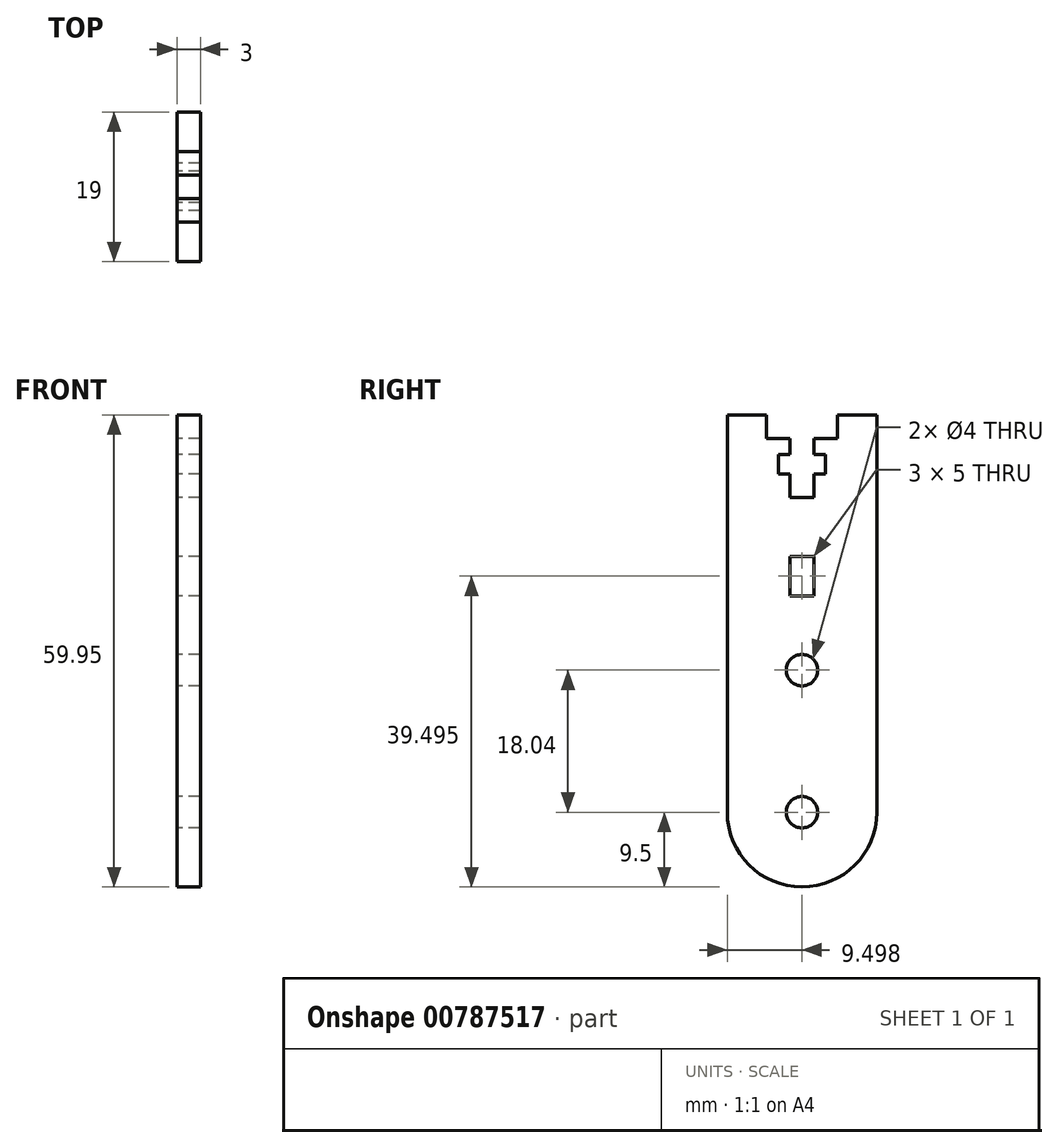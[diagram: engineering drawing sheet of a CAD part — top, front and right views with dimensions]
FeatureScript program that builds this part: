
annotation { "Feature Type Name" : "Feature", "Feature Type Description" : "" }
export const myFeature = defineFeature(function(context is Context, id is Id, definition is map)
    precondition{}
    {
        {
            var Q0;
            Q0=qCreatedBy(makeId("Right.planeOp"),FACE);
            var sketch = newSketch(context, id + "F0", { "sketchPlane" : qUnion([Q0])});
            skLineSegment(sketch, "E0.left", {"start": v(-56.6, 15.77) * mm, "end": v(-56.6, -34.68) * mm});
            skLineSegment(sketch, "E0.right", {"start": v(-37.6, 15.77) * mm, "end": v(-37.6, -34.68) * mm});
            skLineSegment(sketch, "E1", {"start": v(-56.6, 15.77) * mm, "end": v(-51.6, 15.77) * mm});
            skLineSegment(sketch, "E2", {"start": v(-51.6, 15.77) * mm, "end": v(-51.6, 12.77) * mm});
            skLineSegment(sketch, "E3", {"start": v(-51.6, 12.77) * mm, "end": v(-48.6, 12.77) * mm});
            skLineSegment(sketch, "E4", {"start": v(-48.6, 12.77) * mm, "end": v(-48.6, 10.77) * mm});
            skLineSegment(sketch, "E5", {"start": v(-48.6, 10.77) * mm, "end": v(-50.1, 10.77) * mm});
            skLineSegment(sketch, "E6", {"start": v(-50.1, 10.77) * mm, "end": v(-50.1, 8.27) * mm});
            skLineSegment(sketch, "E7", {"start": v(-50.1, 8.27) * mm, "end": v(-48.6, 8.27) * mm});
            skLineSegment(sketch, "E8", {"start": v(-48.6, 8.27) * mm, "end": v(-48.6, 5.27) * mm});
            skLineSegment(sketch, "E9", {"start": v(-48.6, 5.27) * mm, "end": v(-45.6, 5.27) * mm});
            skLineSegment(sketch, "E10", {"start": v(-45.6, 5.27) * mm, "end": v(-45.6, 8.27) * mm});
            skLineSegment(sketch, "E11", {"start": v(-45.6, 8.27) * mm, "end": v(-44.1, 8.27) * mm});
            skLineSegment(sketch, "E12", {"start": v(-44.1, 8.27) * mm, "end": v(-44.1, 10.77) * mm});
            skLineSegment(sketch, "E13", {"start": v(-44.1, 10.77) * mm, "end": v(-45.6, 10.77) * mm});
            skLineSegment(sketch, "E14", {"start": v(-45.6, 10.77) * mm, "end": v(-45.6, 12.77) * mm});
            skLineSegment(sketch, "E15", {"start": v(-45.6, 12.77) * mm, "end": v(-42.6, 12.77) * mm});
            skLineSegment(sketch, "E16", {"start": v(-42.6, 12.77) * mm, "end": v(-42.6, 15.77) * mm});
            skLineSegment(sketch, "E17", {"start": v(-42.6, 15.77) * mm, "end": v(-37.6, 15.77) * mm});
            skCircle(sketch, "E18", {"center": v(-47.1, -34.68) * mm, "radius": 2 * mm});
            skCircle(sketch, "E19", {"center": v(-47.1, -16.64) * mm, "radius": 2 * mm});
            skArc(sketch, "E20", {"start": v(-56.6, -34.68) * mm, "mid": v(-47.1, -44.18) * mm, "end": v(-37.6, -34.68) * mm});
            skLineSegment(sketch, "E21", {"start": v(-47.1, -14.64) * mm, "end": v(-47.1, 5.27) * mm, "construction": true});
            skLineSegment(sketch, "E22.bottom", {"start": v(-48.6, -2.19) * mm, "end": v(-45.6, -2.19) * mm});
            skLineSegment(sketch, "E22.top", {"start": v(-48.6, -7.19) * mm, "end": v(-45.6, -7.19) * mm});
            skLineSegment(sketch, "E22.left", {"start": v(-48.6, -2.19) * mm, "end": v(-48.6, -7.19) * mm});
            skLineSegment(sketch, "E22.right", {"start": v(-45.6, -2.19) * mm, "end": v(-45.6, -7.19) * mm});
            skPoint(sketch, "E22.middle", {"position": v(-47.1, -4.69) * mm});
            skSolve(sketch);
        }
        {
            var Q0;
            Q0=makeQuery(id+"F0.imprint","IMPRINT",FACE,{"disambiguationData":[TD([[makeQuery(id+"F0.imprint","IMPRINT",EDGE,{"derivedFrom":sQuery(id+"F0.wireOp",EDGE,"E0.left")}),1.0]])]});
            extrude(context, id + "F1", {"entities" : qUnion([Q0]), "depth" : 3 * mm, "offsetDistance" : 25.4 * mm});
        }
    });
